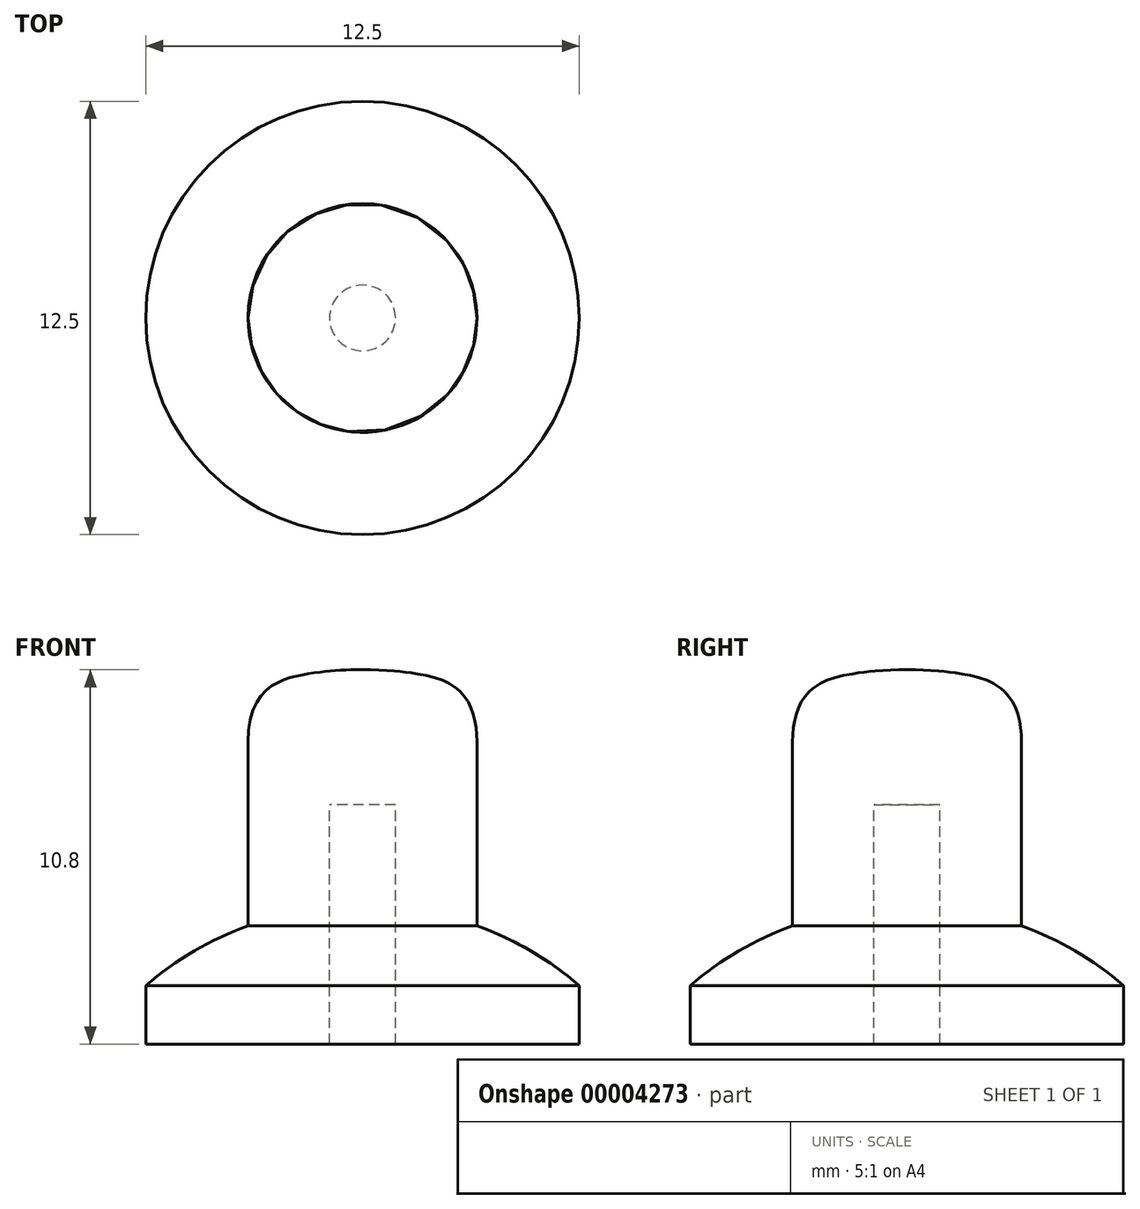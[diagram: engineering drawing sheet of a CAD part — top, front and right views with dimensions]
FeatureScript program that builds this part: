
annotation { "Feature Type Name" : "Feature", "Feature Type Description" : "" }
export const myFeature = defineFeature(function(context is Context, id is Id, definition is map)
    precondition{}
    {
        {
            var Q0;
            Q0=qCreatedBy(makeId("Front.planeOp"),FACE);
            var sketch = newSketch(context, id + "F0", { "sketchPlane" : qUnion([Q0])});
            skLineSegment(sketch, "E0", {"start": v(-0.95, 0) * mm, "end": v(-6.25, 0) * mm});
            skLineSegment(sketch, "E1", {"start": v(-6.25, 0) * mm, "end": v(-6.25, 4) * mm});
            skLineSegment(sketch, "E2", {"start": v(-6.25, 4) * mm, "end": v(-3.3, 4) * mm});
            skLineSegment(sketch, "E3", {"start": v(-4.77, 4) * mm, "end": v(-4.77, 10.8) * mm, "construction": true});
            skLineSegment(sketch, "E4", {"start": v(-3.3, 4) * mm, "end": v(-3.3, 8.72) * mm});
            skLineSegment(sketch, "E5", {"start": v(0, 9.18) * mm, "end": v(-3.3, 9.18) * mm, "construction": true});
            skFitSpline(sketch, "E6", {"points": [v(-3.3, 8.72) * mm, v(-1.56, 10.68) * mm, v(0, 10.8) * mm], "startDerivative": vector(0, 8.64) * mm, "endDerivative": vector(3.96, 0) * mm});
            skLineSegment(sketch, "E7", {"start": v(-4.77, 10.8) * mm, "end": v(0, 10.8) * mm, "construction": true});
            skLineSegment(sketch, "E8", {"start": v(0, 10.8) * mm, "end": v(0, 6.9) * mm});
            skLineSegment(sketch, "E9", {"start": v(0, 6.9) * mm, "end": v(-0.95, 6.9) * mm});
            skLineSegment(sketch, "E10", {"start": v(-0.95, 6.9) * mm, "end": v(-0.95, 0) * mm});
            skPoint(sketch, "E11.orphan", {"position": v(0, 0) * mm});
            skLineSegment(sketch, "E12", {"start": v(-6.25, 1.2) * mm, "end": v(0, 1.2) * mm, "construction": true});
            skLineSegment(sketch, "E13", {"start": v(-3.3, 4) * mm, "end": v(-3.3, 0) * mm});
            skPoint(sketch, "E14", {"position": v(0, 4) * mm});
            skCircle(sketch, "E15", {"center": v(0, -5.61) * mm, "radius": 9.61 * mm});
            skSolve(sketch);
        }
        {
            var Q0;
            Q0=makeQuery(id+"F0.imprint","IMPRINT",FACE,{"disambiguationData":[TD([[makeQuery(id+"F0.imprint","IMPRINT",EDGE,{"derivedFrom":sQuery(id+"F0.wireOp",EDGE,"E0")}),-1.0]])]});
            var Q1;
            Q1=sQuery(id+"F0.wireOp",EDGE,"E8");
            revolve(context, id + "F1", {"entities" : qUnion([Q0]), "axis" : qUnion([Q1]), "revolveType" : RevolveType.FULL});
        }
        {
            var Q0;
            Q0=makeQuery(id+"F0.imprint","IMPRINT",FACE,{"disambiguationData":[TD([[makeQuery(id+"F0.imprint","IMPRINT",EDGE,{"derivedFrom":sQuery(id+"F0.wireOp",EDGE,"E4")}),-1.0]])]});
            var Q1;
            Q1=sQuery(id+"F0.wireOp",EDGE,"E8");
            revolve(context, id + "F2", {"operationType" : NewBodyOperationType.ADD, "entities" : qUnion([Q0]), "axis" : qUnion([Q1]), "revolveType" : RevolveType.FULL});
        }
    });
